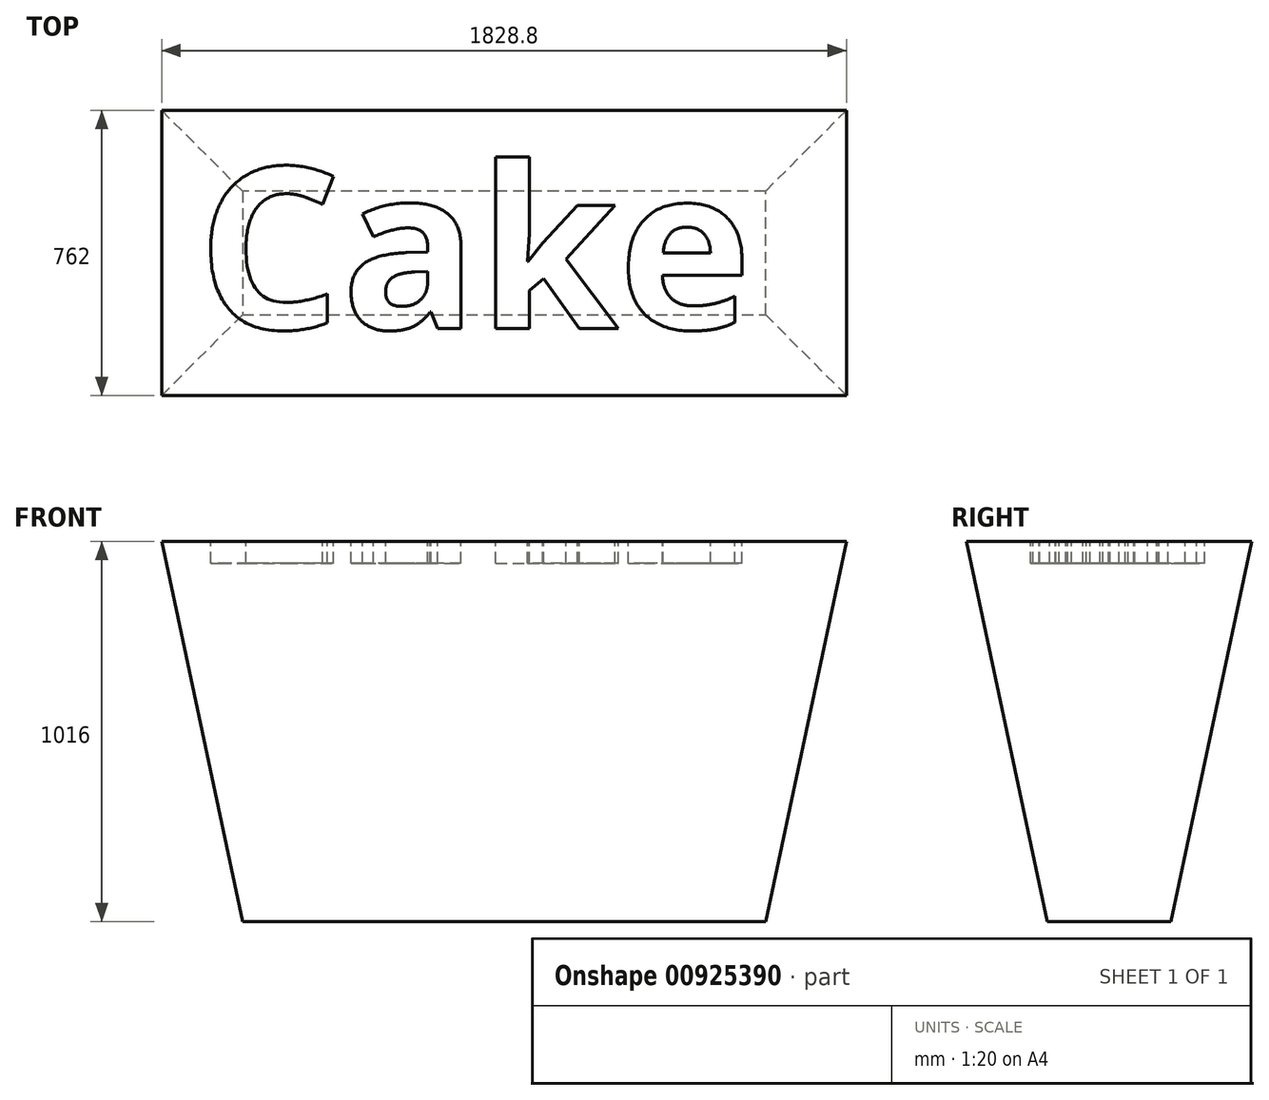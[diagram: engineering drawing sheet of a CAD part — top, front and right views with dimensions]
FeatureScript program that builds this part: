
annotation { "Feature Type Name" : "Feature", "Feature Type Description" : "" }
export const myFeature = defineFeature(function(context is Context, id is Id, definition is map)
    precondition{}
    {
        {
            var Q0;
            Q0=qCreatedBy(makeId("Top.planeOp"),FACE);
            var sketch = newSketch(context, id + "F0", { "sketchPlane" : qUnion([Q0])});
            skLineSegment(sketch, "E0.bottom", {"start": v(914.4, -381) * mm, "end": v(-914.4, -381) * mm});
            skLineSegment(sketch, "E0.top", {"start": v(914.4, 381) * mm, "end": v(-914.4, 381) * mm});
            skLineSegment(sketch, "E0.left", {"start": v(914.4, -381) * mm, "end": v(914.4, 381) * mm});
            skLineSegment(sketch, "E0.right", {"start": v(-914.4, -381) * mm, "end": v(-914.4, 381) * mm});
            skPoint(sketch, "E0.middle", {"position": v(0, 0) * mm});
            skSolve(sketch);
        }
        {
            var Q0;
            Q0 = qSketchRegion(id + "F0", true);
            extrude(context, id + "F1", {"entities" : qUnion([Q0]), "oppositeDirection" : true, "depth" : 1016 * mm, "offsetDistance" : 25.4 * mm, "hasDraft" : true, "draftAngle" : 12 * degree, "draftPullDirection" : true});
        }
        {
            var Q0;
            Q0=makeQuery(id+"F1.opExtrude","CAP_FACE",FACE,{"disambiguationData":[OSD([sQuery(id+"F0.wireOp",EDGE,"E0.bottom"),sQuery(id+"F0.wireOp",EDGE,"E0.top"),sQuery(id+"F0.wireOp",EDGE,"E0.left"),sQuery(id+"F0.wireOp",EDGE,"E0.right")])],"isStart":true});
            var sketch = newSketch(context, id + "F2", { "sketchPlane" : qUnion([Q0])});
            skText(sketch, "E1", { "text": "Cake", "fontName": "OpenSans-Bold.ttf"});
            const initialGuessF2  = {"E1": [-0.81841, -0.20255, 1, 0, 0.43448]};
            skSetInitialGuess(sketch, initialGuessF2);
            skSolve(sketch);
        }
        {
            var Q0;
            Q0 = qSketchRegion(id + "F2", true);
            extrude(context, id + "F3", {"entities" : qUnion([Q0]), "operationType" : NewBodyOperationType.REMOVE, "oppositeDirection" : true, "depth" : 58.42 * mm, "offsetDistance" : 25.4 * mm});
        }
    });
